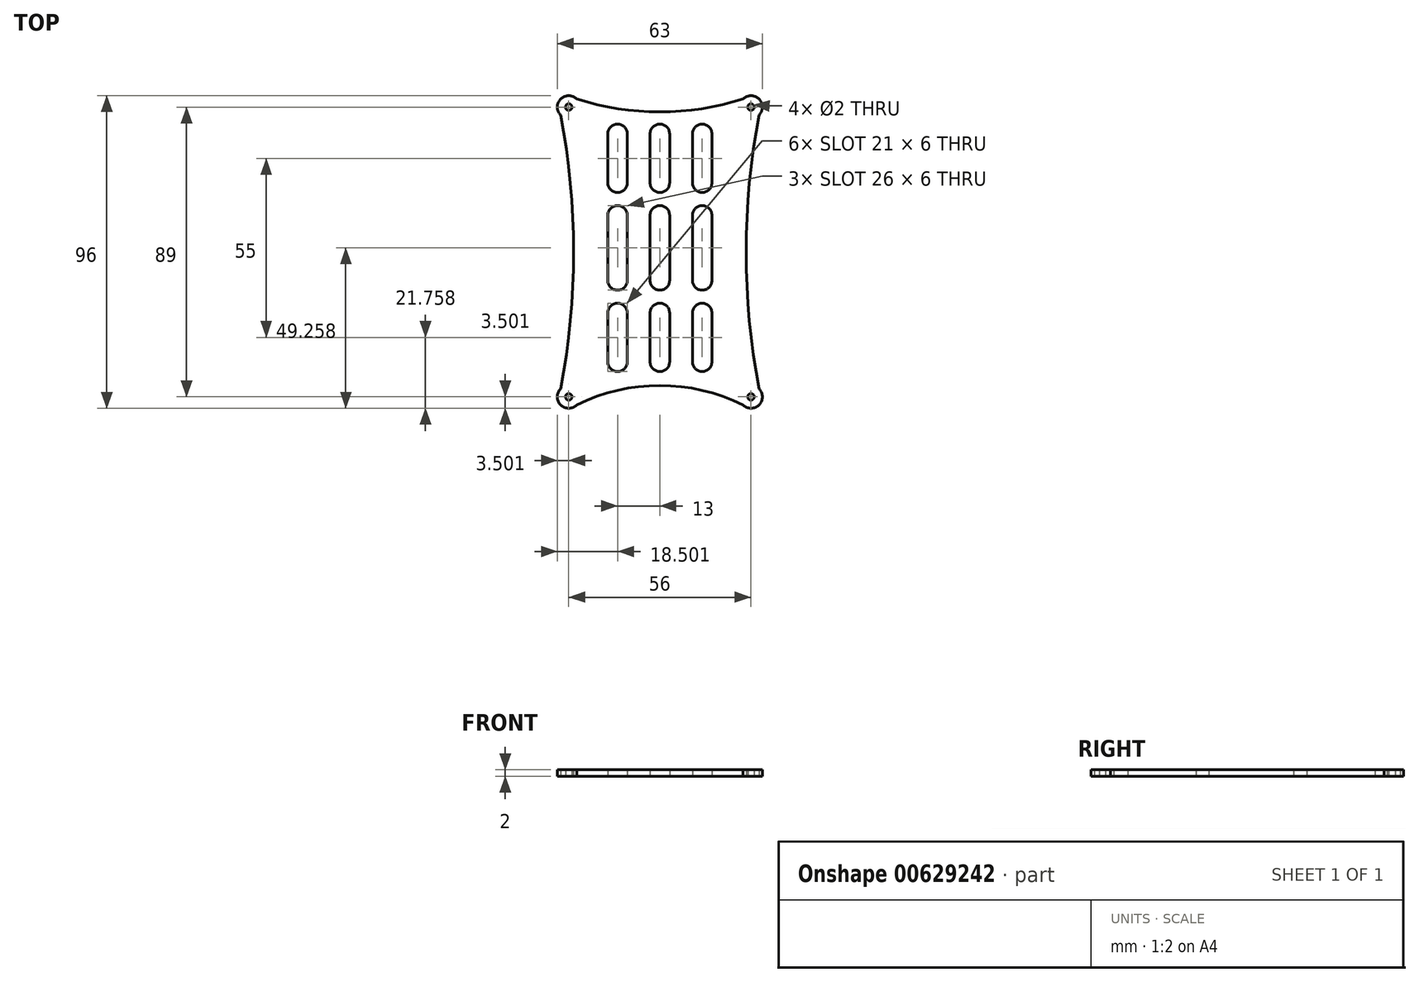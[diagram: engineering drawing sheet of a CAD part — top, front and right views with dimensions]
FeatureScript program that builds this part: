
annotation { "Feature Type Name" : "Feature", "Feature Type Description" : "" }
export const myFeature = defineFeature(function(context is Context, id is Id, definition is map)
    precondition{}
    {
        {
            var Q0;
            Q0=qCreatedBy(makeId("Top.planeOp"),FACE);
            var sketch = newSketch(context, id + "F0", { "sketchPlane" : qUnion([Q0])});
            skLineSegment(sketch, "E0", {"start": v(-22.12, 35.56) * mm, "end": v(17.88, 35.56) * mm, "construction": true});
            skLineSegment(sketch, "E1", {"start": v(17.88, 35.56) * mm, "end": v(17.88, -37.44) * mm, "construction": true});
            skLineSegment(sketch, "E2", {"start": v(17.88, -37.44) * mm, "end": v(-22.12, -37.44) * mm, "construction": true});
            skLineSegment(sketch, "E3", {"start": v(-22.12, -37.44) * mm, "end": v(-22.12, 35.56) * mm, "construction": true});
            skPoint(sketch, "E4", {"position": v(-22.12, 35.56) * mm});
            skPoint(sketch, "E5", {"position": v(17.88, 35.56) * mm});
            skPoint(sketch, "E6", {"position": v(17.88, -37.44) * mm});
            skPoint(sketch, "E7", {"position": v(-22.12, -37.44) * mm});
            skPoint(sketch, "E8", {"position": v(-23.63, 36.57) * mm});
            skPoint(sketch, "E9", {"position": v(21.37, -41.43) * mm});
            skLineSegment(sketch, "E10.bottom", {"start": v(-23.63, 36.57) * mm, "end": v(21.37, 36.57) * mm, "construction": true});
            skLineSegment(sketch, "E10.top", {"start": v(-23.63, -41.43) * mm, "end": v(21.37, -41.43) * mm, "construction": true});
            skLineSegment(sketch, "E10.left", {"start": v(-23.63, 36.57) * mm, "end": v(-23.63, -41.43) * mm, "construction": true});
            skLineSegment(sketch, "E10.right", {"start": v(21.37, 36.57) * mm, "end": v(21.37, -41.43) * mm, "construction": true});
            skLineSegment(sketch, "E11", {"start": v(-23.63, 36.57) * mm, "end": v(-22.12, 35.56) * mm, "construction": true});
            skLineSegment(sketch, "E12", {"start": v(17.88, -37.44) * mm, "end": v(21.37, -41.43) * mm, "construction": true});
            skLineSegment(sketch, "E13", {"start": v(-22.12, -37.44) * mm, "end": v(-23.63, -41.43) * mm, "construction": true});
            skLineSegment(sketch, "E14", {"start": v(17.88, 35.56) * mm, "end": v(21.37, 36.57) * mm, "construction": true});
            skLineSegment(sketch, "E15.bottom", {"start": v(-23.63, 36.57) * mm, "end": v(-27.63, 36.57) * mm, "construction": true});
            skLineSegment(sketch, "E15.top", {"start": v(-23.63, 40.57) * mm, "end": v(-27.63, 40.57) * mm, "construction": true});
            skLineSegment(sketch, "E15.left", {"start": v(-23.63, 36.57) * mm, "end": v(-23.63, 40.57) * mm, "construction": true});
            skLineSegment(sketch, "E15.right", {"start": v(-27.63, 36.57) * mm, "end": v(-27.63, 40.57) * mm, "construction": true});
            skLineSegment(sketch, "E16.bottom", {"start": v(21.37, -41.43) * mm, "end": v(25.37, -41.43) * mm, "construction": true});
            skLineSegment(sketch, "E16.top", {"start": v(21.37, -45.43) * mm, "end": v(25.37, -45.43) * mm, "construction": true});
            skLineSegment(sketch, "E16.left", {"start": v(21.37, -41.43) * mm, "end": v(21.37, -45.43) * mm, "construction": true});
            skLineSegment(sketch, "E16.right", {"start": v(25.37, -41.43) * mm, "end": v(25.37, -45.43) * mm, "construction": true});
            skLineSegment(sketch, "E17", {"start": v(-27.63, 40.57) * mm, "end": v(-23.63, 36.57) * mm, "construction": true});
            skLineSegment(sketch, "E18", {"start": v(25.37, -45.43) * mm, "end": v(21.37, -41.43) * mm, "construction": true});
            skPoint(sketch, "E19", {"position": v(-25.63, 38.57) * mm});
            skPoint(sketch, "E20", {"position": v(23.37, -43.43) * mm});
            skLineSegment(sketch, "E21.bottom", {"start": v(-25.63, 38.57) * mm, "end": v(23.37, 38.57) * mm, "construction": true});
            skLineSegment(sketch, "E21.top", {"start": v(-25.63, -43.43) * mm, "end": v(23.37, -43.43) * mm, "construction": true});
            skLineSegment(sketch, "E21.left", {"start": v(-25.63, 38.57) * mm, "end": v(-25.63, -43.43) * mm, "construction": true});
            skLineSegment(sketch, "E21.right", {"start": v(23.37, 38.57) * mm, "end": v(23.37, -43.43) * mm, "construction": true});
            skLineSegment(sketch, "E22.bottom", {"start": v(-25.63, 38.57) * mm, "end": v(-32.63, 38.57) * mm, "construction": true});
            skLineSegment(sketch, "E22.top", {"start": v(-25.63, 45.57) * mm, "end": v(-32.63, 45.57) * mm, "construction": true});
            skLineSegment(sketch, "E22.left", {"start": v(-25.63, 38.57) * mm, "end": v(-25.63, 45.57) * mm, "construction": true});
            skLineSegment(sketch, "E22.right", {"start": v(-32.63, 38.57) * mm, "end": v(-32.63, 45.57) * mm, "construction": true});
            skLineSegment(sketch, "E23.bottom", {"start": v(23.37, -43.43) * mm, "end": v(30.37, -43.43) * mm, "construction": true});
            skLineSegment(sketch, "E23.top", {"start": v(23.37, -50.43) * mm, "end": v(30.37, -50.43) * mm, "construction": true});
            skLineSegment(sketch, "E23.left", {"start": v(23.37, -43.43) * mm, "end": v(23.37, -50.43) * mm, "construction": true});
            skLineSegment(sketch, "E23.right", {"start": v(30.37, -43.43) * mm, "end": v(30.37, -50.43) * mm, "construction": true});
            skLineSegment(sketch, "E24.bottom", {"start": v(-32.63, -50.43) * mm, "end": v(-25.63, -50.43) * mm, "construction": true});
            skLineSegment(sketch, "E24.top", {"start": v(-32.63, -43.43) * mm, "end": v(-25.63, -43.43) * mm, "construction": true});
            skLineSegment(sketch, "E24.left", {"start": v(-32.63, -50.43) * mm, "end": v(-32.63, -43.43) * mm, "construction": true});
            skLineSegment(sketch, "E24.right", {"start": v(-25.63, -50.43) * mm, "end": v(-25.63, -43.43) * mm, "construction": true});
            skLineSegment(sketch, "E25.bottom", {"start": v(23.37, 38.57) * mm, "end": v(30.37, 38.57) * mm, "construction": true});
            skLineSegment(sketch, "E25.top", {"start": v(23.37, 45.57) * mm, "end": v(30.37, 45.57) * mm, "construction": true});
            skLineSegment(sketch, "E25.left", {"start": v(23.37, 38.57) * mm, "end": v(23.37, 45.57) * mm, "construction": true});
            skLineSegment(sketch, "E25.right", {"start": v(30.37, 38.57) * mm, "end": v(30.37, 45.57) * mm, "construction": true});
            skLineSegment(sketch, "E26", {"start": v(-32.63, 45.57) * mm, "end": v(-25.63, 38.57) * mm, "construction": true});
            skLineSegment(sketch, "E27", {"start": v(30.37, 45.57) * mm, "end": v(23.37, 38.57) * mm, "construction": true});
            skLineSegment(sketch, "E28", {"start": v(-32.63, -50.43) * mm, "end": v(-25.63, -43.43) * mm, "construction": true});
            skLineSegment(sketch, "E29", {"start": v(30.37, -50.43) * mm, "end": v(23.37, -43.43) * mm, "construction": true});
            skPoint(sketch, "E30", {"position": v(-29.13, 42.07) * mm});
            skPoint(sketch, "E31", {"position": v(26.87, 42.07) * mm});
            skPoint(sketch, "E32", {"position": v(26.87, -46.93) * mm});
            skPoint(sketch, "E33", {"position": v(-29.13, -46.93) * mm});
            skCircle(sketch, "E34", {"center": v(-29.13, 42.07) * mm, "radius": 1 * mm});
            skCircle(sketch, "E35", {"center": v(26.87, 42.07) * mm, "radius": 1 * mm});
            skCircle(sketch, "E36", {"center": v(26.87, -46.93) * mm, "radius": 1 * mm});
            skCircle(sketch, "E37", {"center": v(-29.13, -46.93) * mm, "radius": 1 * mm});
            skPoint(sketch, "E38", {"position": v(-1.13, 38.57) * mm});
            skPoint(sketch, "E39", {"position": v(-1.13, -43.43) * mm});
            skPoint(sketch, "E40", {"position": v(-25.63, -46.93) * mm});
            skPoint(sketch, "E41", {"position": v(-29.13, -43.43) * mm});
            skPoint(sketch, "E42", {"position": v(-29.13, 38.57) * mm});
            skPoint(sketch, "E43", {"position": v(-25.63, 42.07) * mm});
            skPoint(sketch, "E44", {"position": v(23.37, 42.07) * mm});
            skPoint(sketch, "E45", {"position": v(26.87, 38.57) * mm});
            skPoint(sketch, "E46", {"position": v(26.87, -43.43) * mm});
            skPoint(sketch, "E47", {"position": v(23.37, -46.93) * mm});
            skPoint(sketch, "E48", {"position": v(-25.63, -2.43) * mm});
            skLineSegment(sketch, "E49", {"start": v(-32.63, 38.57) * mm, "end": v(-25.63, 45.57) * mm, "construction": true});
            skLineSegment(sketch, "E50", {"start": v(23.37, 45.57) * mm, "end": v(30.37, 38.57) * mm, "construction": true});
            skLineSegment(sketch, "E51", {"start": v(23.37, -50.43) * mm, "end": v(30.37, -43.43) * mm, "construction": true});
            skLineSegment(sketch, "E52", {"start": v(-25.63, -50.43) * mm, "end": v(-32.63, -43.43) * mm, "construction": true});
            skPoint(sketch, "E53", {"position": v(-26.65, 44.55) * mm});
            skPoint(sketch, "E54", {"position": v(24.4, 44.55) * mm});
            skPoint(sketch, "E55", {"position": v(24.93, -48.87) * mm});
            skPoint(sketch, "E56", {"position": v(23.37, -2.43) * mm});
            skLineSegment(sketch, "E57", {"start": v(-1.13, 38.57) * mm, "end": v(-1.13, 40.57) * mm, "construction": true});
            skLineSegment(sketch, "E58", {"start": v(23.37, -2.43) * mm, "end": v(25.37, -2.43) * mm, "construction": true});
            skLineSegment(sketch, "E59", {"start": v(-1.13, -43.43) * mm, "end": v(-1.13, -45.43) * mm, "construction": true});
            skLineSegment(sketch, "E60", {"start": v(-25.63, -2.43) * mm, "end": v(-27.63, -2.43) * mm, "construction": true});
            skArc(sketch, "E61", {"start": v(24.4, 44.55) * mm, "mid": v(29.35, 44.55) * mm, "end": v(29.35, 39.6) * mm});
            skArc(sketch, "E62", {"start": v(-26.65, 44.55) * mm, "mid": v(-31.6, 44.55) * mm, "end": v(-31.6, 39.6) * mm});
            skPoint(sketch, "E63", {"position": v(-1.13, 40.57) * mm});
            skArc(sketch, "E64", {"start": v(-26.65, 44.55) * mm, "mid": v(-1.13, 40.57) * mm, "end": v(24.4, 44.55) * mm});
            skLineSegment(sketch, "E65", {"start": v(-1.13, 40.57) * mm, "end": v(-1.13, 60.57) * mm, "construction": true});
            skLineSegment(sketch, "E66", {"start": v(-1.13, 60.57) * mm, "end": v(8.87, 60.57) * mm, "construction": true});
            skLineSegment(sketch, "E67", {"start": v(8.87, 60.57) * mm, "end": v(8.87, 41.17) * mm, "construction": true});
            skLineSegment(sketch, "E68", {"start": v(-1.13, 60.57) * mm, "end": v(-11.13, 60.57) * mm, "construction": true});
            skLineSegment(sketch, "E69", {"start": v(-11.13, 60.57) * mm, "end": v(-11.13, 41.17) * mm, "construction": true});
            skPoint(sketch, "E70", {"position": v(-11.13, 41.17) * mm});
            skPoint(sketch, "E71", {"position": v(-1.13, 60.57) * mm});
            skPoint(sketch, "E72", {"position": v(8.87, 41.17) * mm});
            skPoint(sketch, "E73", {"position": v(-1.13, 50.57) * mm});
            skPoint(sketch, "E74", {"position": v(-11.13, 50.57) * mm});
            skPoint(sketch, "E75", {"position": v(8.87, 50.57) * mm});
            skPoint(sketch, "E76", {"position": v(-19.57, 42.62) * mm});
            skPoint(sketch, "E77", {"position": v(17.31, 42.62) * mm});
            skPoint(sketch, "E78", {"position": v(19.5, -47.45) * mm});
            skPoint(sketch, "E79", {"position": v(-17.39, -47.45) * mm});
            skLineSegment(sketch, "E80", {"start": v(-1.13, -45.43) * mm, "end": v(-1.13, -65.43) * mm, "construction": true});
            skLineSegment(sketch, "E81", {"start": v(-1.13, -65.43) * mm, "end": v(-11.13, -65.43) * mm, "construction": true});
            skLineSegment(sketch, "E82", {"start": v(-11.13, -65.43) * mm, "end": v(-11.13, -46.29) * mm, "construction": true});
            skLineSegment(sketch, "E83", {"start": v(-1.13, -65.43) * mm, "end": v(8.87, -65.43) * mm, "construction": true});
            skLineSegment(sketch, "E84", {"start": v(8.87, -65.43) * mm, "end": v(8.87, -45.77) * mm, "construction": true});
            skPoint(sketch, "E85", {"position": v(-1.13, -55.43) * mm});
            skPoint(sketch, "E86", {"position": v(-1.13, -1.17) * mm});
            skLineSegment(sketch, "E87", {"start": v(-1.13, -1.17) * mm, "end": v(-4.13, -1.17) * mm, "construction": true});
            skLineSegment(sketch, "E88", {"start": v(-4.13, -1.17) * mm, "end": v(-14.13, -1.17) * mm, "construction": true});
            skLineSegment(sketch, "E89", {"start": v(-14.13, -1.17) * mm, "end": v(-20.13, -1.17) * mm, "construction": true});
            skLineSegment(sketch, "E90", {"start": v(-1.13, -1.17) * mm, "end": v(1.87, -1.17) * mm, "construction": true});
            skLineSegment(sketch, "E91", {"start": v(1.87, -1.17) * mm, "end": v(11.87, -1.17) * mm, "construction": true});
            skLineSegment(sketch, "E92", {"start": v(11.87, -1.17) * mm, "end": v(17.87, -1.17) * mm, "construction": true});
            skLineSegment(sketch, "E93", {"start": v(-1.13, -1.17) * mm, "end": v(-1.13, 8.83) * mm, "construction": true});
            skLineSegment(sketch, "E94", {"start": v(-1.13, 8.83) * mm, "end": v(-1.13, 18.83) * mm, "construction": true});
            skLineSegment(sketch, "E95", {"start": v(-1.13, 18.83) * mm, "end": v(-1.13, 33.83) * mm, "construction": true});
            skLineSegment(sketch, "E96", {"start": v(-1.13, -1.17) * mm, "end": v(-1.13, -11.17) * mm, "construction": true});
            skLineSegment(sketch, "E97", {"start": v(-1.13, -11.17) * mm, "end": v(-1.13, -21.17) * mm, "construction": true});
            skLineSegment(sketch, "E98", {"start": v(-1.13, -21.17) * mm, "end": v(-1.13, -36.17) * mm, "construction": true});
            skLineSegment(sketch, "E99", {"start": v(-1.13, 33.83) * mm, "end": v(-22.12, 33.83) * mm, "construction": true});
            skLineSegment(sketch, "E100", {"start": v(-1.13, 33.83) * mm, "end": v(17.88, 33.83) * mm, "construction": true});
            skLineSegment(sketch, "E101", {"start": v(-1.13, 18.83) * mm, "end": v(-22.12, 18.83) * mm, "construction": true});
            skLineSegment(sketch, "E102", {"start": v(-1.13, 18.83) * mm, "end": v(17.88, 18.83) * mm, "construction": true});
            skLineSegment(sketch, "E103", {"start": v(-1.13, 8.83) * mm, "end": v(-22.12, 8.83) * mm, "construction": true});
            skLineSegment(sketch, "E104", {"start": v(-1.13, 8.83) * mm, "end": v(17.88, 8.83) * mm, "construction": true});
            skLineSegment(sketch, "E105", {"start": v(-1.13, -11.17) * mm, "end": v(17.88, -11.17) * mm, "construction": true});
            skLineSegment(sketch, "E106", {"start": v(-1.13, -11.17) * mm, "end": v(-22.12, -11.17) * mm, "construction": true});
            skLineSegment(sketch, "E107", {"start": v(-1.13, -21.17) * mm, "end": v(-22.12, -21.17) * mm, "construction": true});
            skLineSegment(sketch, "E108", {"start": v(-1.13, -21.17) * mm, "end": v(17.88, -21.17) * mm, "construction": true});
            skLineSegment(sketch, "E109", {"start": v(-1.13, -36.17) * mm, "end": v(-22.12, -36.17) * mm, "construction": true});
            skLineSegment(sketch, "E110", {"start": v(-1.13, -36.17) * mm, "end": v(17.88, -36.17) * mm, "construction": true});
            skCircle(sketch, "E111", {"center": v(-1.13, 33.83) * mm, "radius": 3 * mm, "construction": true});
            skCircle(sketch, "E112", {"center": v(-1.13, 18.83) * mm, "radius": 3 * mm, "construction": true});
            skCircle(sketch, "E113", {"center": v(-1.13, 8.83) * mm, "radius": 3 * mm, "construction": true});
            skCircle(sketch, "E114", {"center": v(-1.13, -11.17) * mm, "radius": 3 * mm, "construction": true});
            skCircle(sketch, "E115", {"center": v(-1.13, -21.17) * mm, "radius": 3 * mm, "construction": true});
            skCircle(sketch, "E116", {"center": v(-1.13, -36.17) * mm, "radius": 3 * mm, "construction": true});
            skLineSegment(sketch, "E117", {"start": v(-14.13, -1.17) * mm, "end": v(-14.13, 33.83) * mm, "construction": true});
            skLineSegment(sketch, "E118", {"start": v(-14.13, -1.17) * mm, "end": v(-14.13, -36.17) * mm, "construction": true});
            skLineSegment(sketch, "E119", {"start": v(11.87, -1.17) * mm, "end": v(11.87, 33.83) * mm, "construction": true});
            skPoint(sketch, "E120", {"position": v(-14.13, 18.83) * mm});
            skLineSegment(sketch, "E121", {"start": v(11.87, -1.17) * mm, "end": v(11.87, -36.17) * mm, "construction": true});
            skPoint(sketch, "E122", {"position": v(-14.13, -21.17) * mm});
            skPoint(sketch, "E123", {"position": v(11.87, -21.17) * mm});
            skPoint(sketch, "E124", {"position": v(11.87, -36.17) * mm});
            skPoint(sketch, "E125", {"position": v(-14.13, -36.17) * mm});
            skPoint(sketch, "E126", {"position": v(11.87, 18.83) * mm});
            skPoint(sketch, "E127", {"position": v(11.87, 8.83) * mm});
            skPoint(sketch, "E128", {"position": v(11.87, -11.17) * mm});
            skPoint(sketch, "E129", {"position": v(-14.13, -11.17) * mm});
            skPoint(sketch, "E130", {"position": v(-14.13, 8.83) * mm});
            skCircle(sketch, "E131", {"center": v(-14.13, 33.83) * mm, "radius": 3 * mm, "construction": true});
            skCircle(sketch, "E132", {"center": v(-14.13, 18.83) * mm, "radius": 3 * mm, "construction": true});
            skCircle(sketch, "E133", {"center": v(-14.13, 8.83) * mm, "radius": 3 * mm, "construction": true});
            skCircle(sketch, "E134", {"center": v(-14.13, -11.17) * mm, "radius": 3 * mm, "construction": true});
            skCircle(sketch, "E135", {"center": v(-14.13, -21.17) * mm, "radius": 3 * mm, "construction": true});
            skCircle(sketch, "E136", {"center": v(11.87, 33.83) * mm, "radius": 3 * mm, "construction": true});
            skCircle(sketch, "E137", {"center": v(11.87, 18.83) * mm, "radius": 3 * mm, "construction": true});
            skCircle(sketch, "E138", {"center": v(11.87, 8.83) * mm, "radius": 3 * mm, "construction": true});
            skCircle(sketch, "E139", {"center": v(11.87, -11.17) * mm, "radius": 3 * mm, "construction": true});
            skCircle(sketch, "E140", {"center": v(11.87, -21.17) * mm, "radius": 3 * mm, "construction": true});
            skCircle(sketch, "E141", {"center": v(-14.13, -36.17) * mm, "radius": 3 * mm, "construction": true});
            skCircle(sketch, "E142", {"center": v(11.87, -36.17) * mm, "radius": 3 * mm, "construction": true});
            skPoint(sketch, "E143", {"position": v(14.87, 33.83) * mm});
            skPoint(sketch, "E144", {"position": v(1.87, 33.83) * mm});
            skPoint(sketch, "E145", {"position": v(8.87, 33.83) * mm});
            skPoint(sketch, "E146", {"position": v(-17.13, 33.83) * mm});
            skPoint(sketch, "E147", {"position": v(-11.13, 33.83) * mm});
            skPoint(sketch, "E148", {"position": v(-4.13, 33.83) * mm});
            skArc(sketch, "E149", {"start": v(-17.13, 33.83) * mm, "mid": v(-14.13, 36.83) * mm, "end": v(-11.13, 33.83) * mm, "construction": true});
            skArc(sketch, "E150", {"start": v(-4.13, 33.83) * mm, "mid": v(-1.13, 36.83) * mm, "end": v(1.87, 33.83) * mm, "construction": true});
            skArc(sketch, "E151", {"start": v(8.87, 33.83) * mm, "mid": v(11.87, 36.83) * mm, "end": v(14.87, 33.83) * mm, "construction": true});
            skArc(sketch, "E152", {"start": v(14.87, 18.83) * mm, "mid": v(11.87, 15.83) * mm, "end": v(8.87, 18.83) * mm, "construction": true});
            skArc(sketch, "E153", {"start": v(1.87, 18.83) * mm, "mid": v(-1.13, 15.83) * mm, "end": v(-4.13, 18.83) * mm, "construction": true});
            skArc(sketch, "E154", {"start": v(-11.13, 18.83) * mm, "mid": v(-14.13, 15.83) * mm, "end": v(-17.13, 18.83) * mm, "construction": true});
            skLineSegment(sketch, "E155", {"start": v(-17.13, 33.83) * mm, "end": v(-17.13, 18.83) * mm});
            skLineSegment(sketch, "E156", {"start": v(-11.13, 33.83) * mm, "end": v(-11.13, 18.83) * mm});
            skLineSegment(sketch, "E157", {"start": v(-4.13, 33.83) * mm, "end": v(-4.13, 18.83) * mm});
            skLineSegment(sketch, "E158", {"start": v(1.87, 33.83) * mm, "end": v(1.87, 18.83) * mm});
            skLineSegment(sketch, "E159", {"start": v(8.87, 33.83) * mm, "end": v(8.87, 18.83) * mm});
            skLineSegment(sketch, "E160", {"start": v(14.87, 33.83) * mm, "end": v(14.87, 18.83) * mm});
            skArc(sketch, "E161", {"start": v(-17.13, 8.83) * mm, "mid": v(-14.13, 11.83) * mm, "end": v(-11.13, 8.83) * mm});
            skArc(sketch, "E162", {"start": v(-4.13, 8.83) * mm, "mid": v(-1.13, 11.83) * mm, "end": v(1.87, 8.83) * mm});
            skArc(sketch, "E163", {"start": v(8.87, 8.83) * mm, "mid": v(11.87, 11.83) * mm, "end": v(14.87, 8.83) * mm});
            skArc(sketch, "E164", {"start": v(-17.13, -11.17) * mm, "mid": v(-14.13, -14.17) * mm, "end": v(-11.13, -11.17) * mm});
            skArc(sketch, "E165", {"start": v(-4.13, -11.17) * mm, "mid": v(-1.13, -14.17) * mm, "end": v(1.87, -11.17) * mm});
            skArc(sketch, "E166", {"start": v(8.87, -11.17) * mm, "mid": v(11.87, -14.17) * mm, "end": v(14.87, -11.17) * mm});
            skLineSegment(sketch, "E167", {"start": v(-17.13, 8.83) * mm, "end": v(-17.13, -11.17) * mm});
            skLineSegment(sketch, "E168", {"start": v(-11.13, 8.83) * mm, "end": v(-11.13, -11.17) * mm});
            skLineSegment(sketch, "E169", {"start": v(-4.13, 8.83) * mm, "end": v(-4.13, -11.17) * mm});
            skLineSegment(sketch, "E170", {"start": v(1.87, 8.83) * mm, "end": v(1.87, -11.17) * mm});
            skLineSegment(sketch, "E171", {"start": v(8.87, 8.83) * mm, "end": v(8.87, -11.17) * mm});
            skLineSegment(sketch, "E172", {"start": v(14.87, 8.83) * mm, "end": v(14.87, -11.17) * mm});
            skArc(sketch, "E173", {"start": v(14.87, 18.83) * mm, "mid": v(11.87, 15.83) * mm, "end": v(8.87, 18.83) * mm});
            skArc(sketch, "E174", {"start": v(1.87, 18.83) * mm, "mid": v(-1.13, 15.83) * mm, "end": v(-4.13, 18.83) * mm});
            skArc(sketch, "E175", {"start": v(8.87, 33.83) * mm, "mid": v(11.87, 36.83) * mm, "end": v(14.87, 33.83) * mm});
            skArc(sketch, "E176", {"start": v(-4.13, 33.83) * mm, "mid": v(-1.13, 36.83) * mm, "end": v(1.87, 33.83) * mm});
            skArc(sketch, "E177", {"start": v(-17.13, 33.83) * mm, "mid": v(-14.13, 36.83) * mm, "end": v(-11.13, 33.83) * mm});
            skArc(sketch, "E178", {"start": v(-17.13, 18.83) * mm, "mid": v(-14.13, 15.83) * mm, "end": v(-11.13, 18.83) * mm});
            skArc(sketch, "E179", {"start": v(-17.13, -21.17) * mm, "mid": v(-14.13, -18.17) * mm, "end": v(-11.13, -21.17) * mm});
            skArc(sketch, "E180", {"start": v(-4.13, -21.17) * mm, "mid": v(-1.13, -18.17) * mm, "end": v(1.87, -21.17) * mm});
            skArc(sketch, "E181", {"start": v(8.87, -21.17) * mm, "mid": v(11.87, -18.17) * mm, "end": v(14.87, -21.17) * mm});
            skArc(sketch, "E182", {"start": v(-17.13, -36.17) * mm, "mid": v(-14.13, -39.17) * mm, "end": v(-11.13, -36.17) * mm});
            skArc(sketch, "E183", {"start": v(-4.13, -36.17) * mm, "mid": v(-1.13, -39.17) * mm, "end": v(1.87, -36.17) * mm});
            skArc(sketch, "E184", {"start": v(14.87, -36.17) * mm, "mid": v(11.87, -39.17) * mm, "end": v(8.87, -36.17) * mm});
            skLineSegment(sketch, "E185", {"start": v(-17.13, -21.17) * mm, "end": v(-17.13, -36.17) * mm});
            skLineSegment(sketch, "E186", {"start": v(-11.13, -21.17) * mm, "end": v(-11.13, -36.17) * mm});
            skLineSegment(sketch, "E187", {"start": v(-4.13, -21.17) * mm, "end": v(-4.13, -36.17) * mm});
            skLineSegment(sketch, "E188", {"start": v(1.87, -21.17) * mm, "end": v(1.87, -36.17) * mm});
            skLineSegment(sketch, "E189", {"start": v(8.87, -21.17) * mm, "end": v(8.87, -36.17) * mm});
            skLineSegment(sketch, "E190", {"start": v(14.87, -21.17) * mm, "end": v(14.87, -36.17) * mm});
            skPoint(sketch, "E191", {"position": v(29.35, 39.6) * mm});
            skPoint(sketch, "E192", {"position": v(-31.6, 39.6) * mm});
            skPoint(sketch, "E193", {"position": v(25.37, -2.43) * mm});
            skPoint(sketch, "E194", {"position": v(-27.63, -2.43) * mm});
            skPoint(sketch, "E195", {"position": v(-31.6, -44.45) * mm});
            skPoint(sketch, "E196", {"position": v(29.35, -44.45) * mm});
            skArc(sketch, "E197", {"start": v(29.35, 39.6) * mm, "mid": v(25.37, -2.43) * mm, "end": v(29.35, -44.45) * mm});
            skArc(sketch, "E198", {"start": v(-31.6, -44.45) * mm, "mid": v(-27.63, -2.43) * mm, "end": v(-31.6, 39.6) * mm});
            skPoint(sketch, "E199", {"position": v(24.4, -49.4) * mm});
            skPoint(sketch, "E200", {"position": v(-26.65, -49.4) * mm});
            skPoint(sketch, "E201", {"position": v(-32.63, -46.93) * mm});
            skPoint(sketch, "E202", {"position": v(30.37, -46.93) * mm});
            skArc(sketch, "E203", {"start": v(24.4, -49.4) * mm, "mid": v(-1.13, -43.43) * mm, "end": v(-26.65, -49.4) * mm});
            skArc(sketch, "E204", {"start": v(-31.6, -44.45) * mm, "mid": v(-31.6, -49.4) * mm, "end": v(-26.65, -49.4) * mm});
            skArc(sketch, "E205", {"start": v(29.35, -44.45) * mm, "mid": v(29.35, -49.4) * mm, "end": v(24.4, -49.4) * mm});
            skSolve(sketch);
        }
        {
            var Q0;
            Q0=makeQuery(id+"F0.imprint","IMPRINT",FACE,{"disambiguationData":[TD([[makeQuery(id+"F0.imprint","IMPRINT",EDGE,{"derivedFrom":sQuery(id+"F0.wireOp",EDGE,"E34")}),-1.0]])]});
            extrude(context, id + "F1", {"entities" : qUnion([Q0]), "depth" : 2 * mm, "offsetDistance" : 25 * mm});
        }
    });
